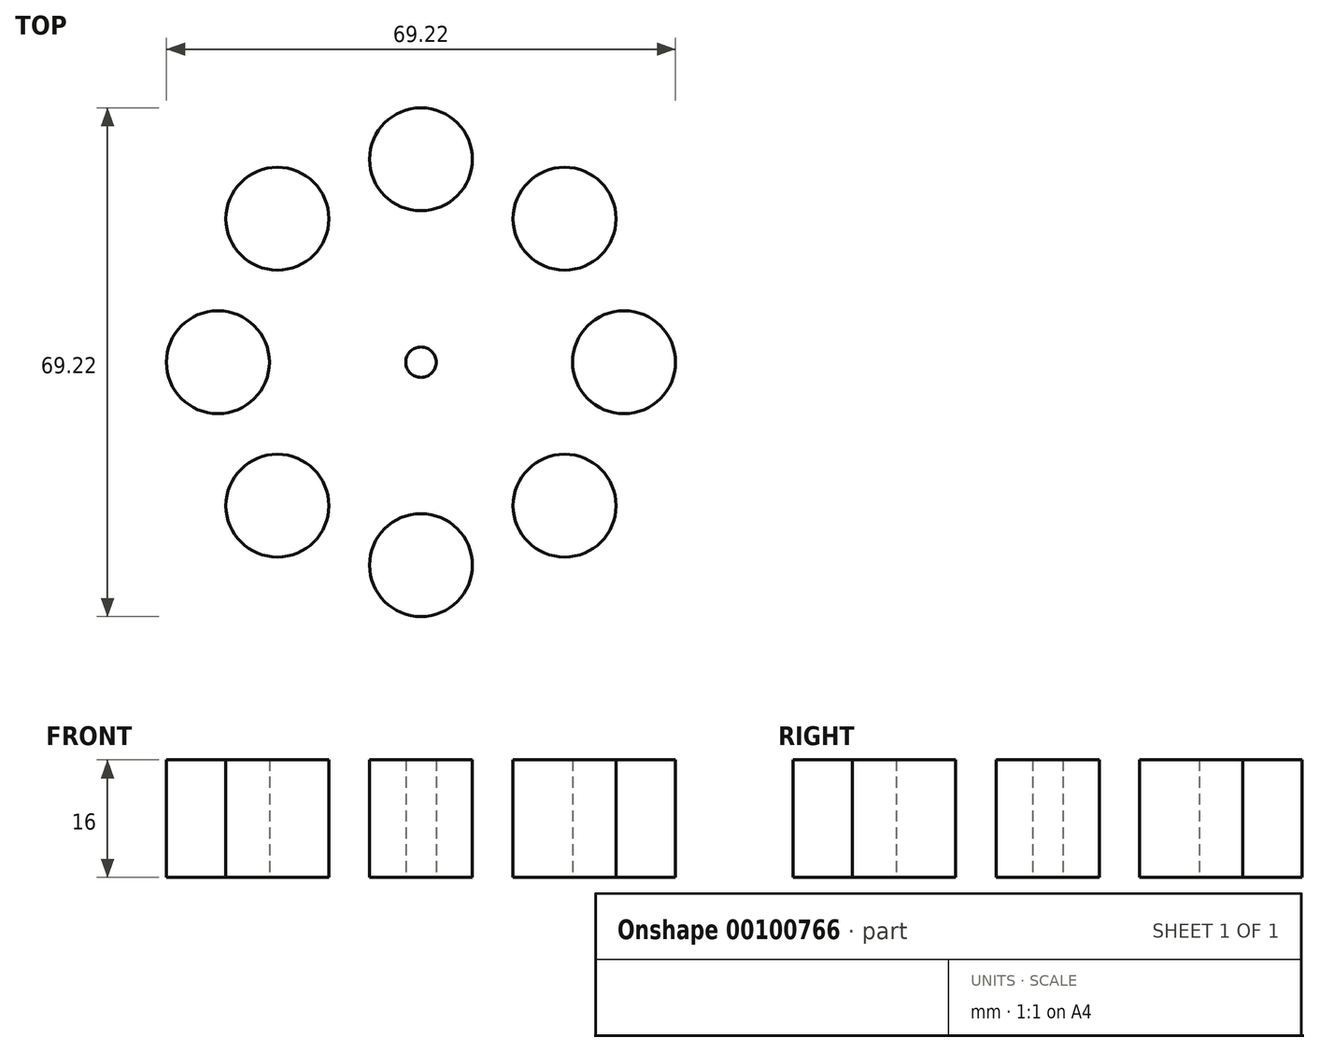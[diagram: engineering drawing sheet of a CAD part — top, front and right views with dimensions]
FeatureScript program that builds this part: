
annotation { "Feature Type Name" : "Feature", "Feature Type Description" : "" }
export const myFeature = defineFeature(function(context is Context, id is Id, definition is map)
    precondition{}
    {
        {
            var Q0;
            Q0=qCreatedBy(makeId("Top.planeOp"),FACE);
            var sketch = newSketch(context, id + "F0", { "sketchPlane" : qUnion([Q0])});
            skCircle(sketch, "E0", {"center": v(0, 0) * mm, "radius": 20.5 * mm, "construction": true});
            skCircle(sketch, "E1", {"center": v(0, -0.27) * mm, "radius": 35 * mm, "construction": true});
            skLineSegment(sketch, "E2", {"start": v(0, 34.73) * mm, "end": v(0, 20.5) * mm, "construction": true});
            skCircle(sketch, "E3", {"center": v(0, 27.61) * mm, "radius": 7 * mm});
            skCircle(sketch, "E4.1.0", {"center": v(-19.53, 19.53) * mm, "radius": 7 * mm});
            skCircle(sketch, "E4.2.0", {"center": v(-27.61, 0) * mm, "radius": 7 * mm});
            skCircle(sketch, "E4.3.0", {"center": v(-19.53, -19.53) * mm, "radius": 7 * mm});
            skCircle(sketch, "E4.4.0", {"center": v(0, -27.61) * mm, "radius": 7 * mm});
            skCircle(sketch, "E4.5.0", {"center": v(19.53, -19.53) * mm, "radius": 7 * mm});
            skCircle(sketch, "E4.6.0", {"center": v(27.61, 0) * mm, "radius": 7 * mm});
            skCircle(sketch, "E4.7.0", {"center": v(19.53, 19.53) * mm, "radius": 7 * mm});
            skLineSegment(sketch, "E5", {"start": v(19.53, 19.53) * mm, "end": v(0, 0) * mm, "construction": true});
            skLineSegment(sketch, "E6", {"start": v(0, 0) * mm, "end": v(27.61, 0) * mm, "construction": true});
            skLineSegment(sketch, "E7", {"start": v(27.61, 0) * mm, "end": v(19.53, 19.53) * mm, "construction": true});
            skCircle(sketch, "E8", {"center": v(0, 0) * mm, "radius": 2.07 * mm});
            skSolve(sketch);
        }
        {
            var Q0;
            Q0=makeQuery(id+"F0.imprint","IMPRINT",FACE,{"disambiguationData":[TD([[makeQuery(id+"F0.imprint","IMPRINT",EDGE,{"derivedFrom":sQuery(id+"F0.wireOp",EDGE,"E3")}),1.0]])]});
            var Q1;
            Q1=makeQuery(id+"F0.imprint","IMPRINT",FACE,{"disambiguationData":[TD([[makeQuery(id+"F0.imprint","IMPRINT",EDGE,{"derivedFrom":sQuery(id+"F0.wireOp",EDGE,"E4.1.0")}),1.0]])]});
            var Q2;
            Q2=makeQuery(id+"F0.imprint","IMPRINT",FACE,{"disambiguationData":[TD([[makeQuery(id+"F0.imprint","IMPRINT",EDGE,{"derivedFrom":sQuery(id+"F0.wireOp",EDGE,"E4.2.0")}),1.0]])]});
            var Q3;
            Q3=makeQuery(id+"F0.imprint","IMPRINT",FACE,{"disambiguationData":[TD([[makeQuery(id+"F0.imprint","IMPRINT",EDGE,{"derivedFrom":sQuery(id+"F0.wireOp",EDGE,"E4.3.0")}),1.0]])]});
            var Q4;
            Q4=makeQuery(id+"F0.imprint","IMPRINT",FACE,{"disambiguationData":[TD([[makeQuery(id+"F0.imprint","IMPRINT",EDGE,{"derivedFrom":sQuery(id+"F0.wireOp",EDGE,"E4.4.0")}),1.0]])]});
            var Q5;
            Q5=makeQuery(id+"F0.imprint","IMPRINT",FACE,{"disambiguationData":[TD([[makeQuery(id+"F0.imprint","IMPRINT",EDGE,{"derivedFrom":sQuery(id+"F0.wireOp",EDGE,"E4.5.0")}),1.0]])]});
            var Q6;
            Q6=makeQuery(id+"F0.imprint","IMPRINT",FACE,{"disambiguationData":[TD([[makeQuery(id+"F0.imprint","IMPRINT",EDGE,{"derivedFrom":sQuery(id+"F0.wireOp",EDGE,"E4.6.0")}),1.0]])]});
            var Q7;
            Q7=makeQuery(id+"F0.imprint","IMPRINT",FACE,{"disambiguationData":[TD([[makeQuery(id+"F0.imprint","IMPRINT",EDGE,{"derivedFrom":sQuery(id+"F0.wireOp",EDGE,"E4.7.0")}),1.0]])]});
            var Q8;
            Q8=makeQuery(id+"F0.imprint","IMPRINT",FACE,{"disambiguationData":[TD([[makeQuery(id+"F0.imprint","IMPRINT",EDGE,{"derivedFrom":sQuery(id+"F0.wireOp",EDGE,"E8")}),1.0]])]});
            extrude(context, id + "F1", {"entities" : qUnion([Q0, Q1, Q2, Q3, Q4, Q5, Q6, Q7, Q8]), "depth" : 16 * mm});
        }
    });
